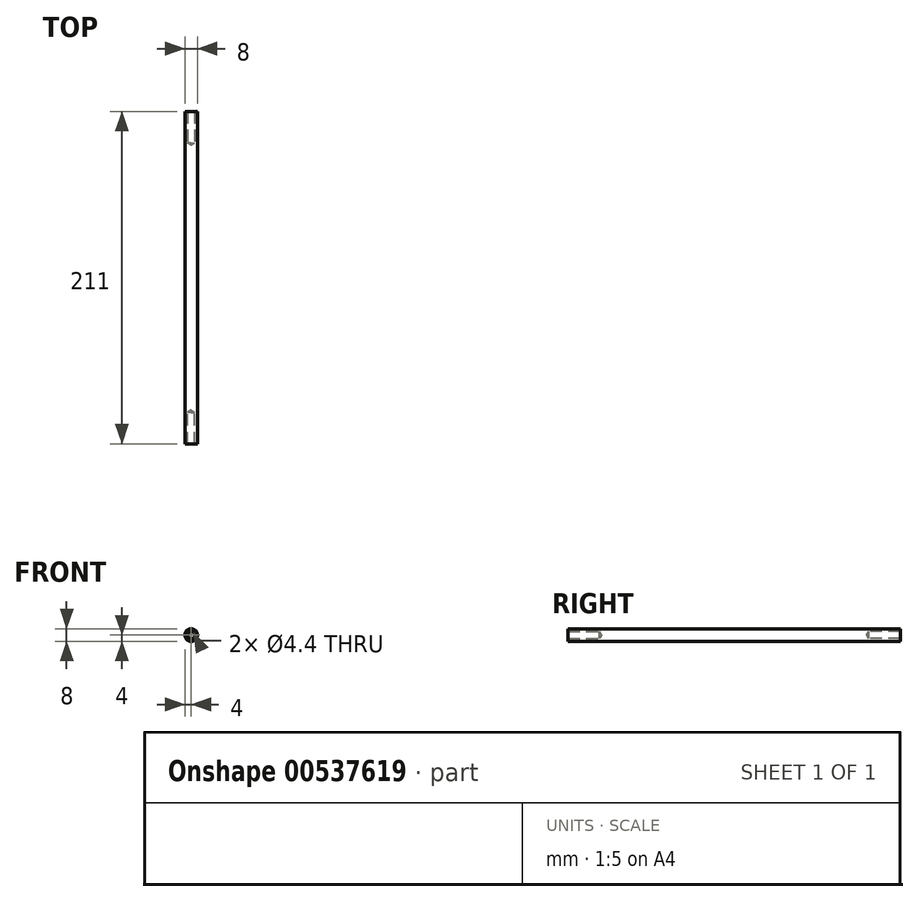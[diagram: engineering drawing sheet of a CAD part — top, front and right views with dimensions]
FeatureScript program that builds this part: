
annotation { "Feature Type Name" : "Feature", "Feature Type Description" : "" }
export const myFeature = defineFeature(function(context is Context, id is Id, definition is map)
    precondition{}
    {
        {
            var Q0;
            Q0=qCreatedBy(makeId("Front.planeOp"),FACE);
            var sketch = newSketch(context, id + "F0", { "sketchPlane" : qUnion([Q0])});
            skCircle(sketch, "E0", {"center": v(0, 0) * mm, "radius": 4 * mm});
            skSolve(sketch);
        }
        {
            var Q0;
            Q0=makeQuery(id+"F0.imprint","IMPRINT",FACE,{"disambiguationData":[TD([[makeQuery(id+"F0.imprint","IMPRINT",EDGE,{"derivedFrom":sQuery(id+"F0.wireOp",EDGE,"E0")}),1.0]])]});
            extrude(context, id + "F1", {"entities" : qUnion([Q0]), "flatOperationType" : FlatOperationType.REMOVE, "depth" : 211 * mm, "offsetDistance" : 25 * mm, "domain" : OperationDomain.MODEL});
        }
        {
            var Q0;
            Q0=makeQuery(id+"F1.opExtrude","CAP_FACE",FACE,{"disambiguationData":[OSD([sQuery(id+"F0.wireOp",EDGE,"E0")])],"isStart":false});
            var sketch = newSketch(context, id + "F2", { "sketchPlane" : qUnion([Q0])});
            skPoint(sketch, "E1", {"position": v(0, 0) * mm});
            skSolve(sketch);
        }
        {
            var Q0;
            Q0=makeQuery(id+"F1.opExtrude","CAP_FACE",FACE,{"disambiguationData":[OSD([sQuery(id+"F0.wireOp",EDGE,"E0")])],"isStart":true});
            var sketch = newSketch(context, id + "F3", { "sketchPlane" : qUnion([Q0])});
            skPoint(sketch, "E2", {"position": v(0, 0) * mm});
            skSolve(sketch);
        }
        {
            var Q0;
            Q0=sQuery(id+"F3.wireOp",VERTEX,"E2");
            var Q1;
            Q1=sQuery(id+"F2.wireOp",VERTEX,"E1");
            var Q2;
            Q2=makeQuery(id+"F1.opExtrude","SWEPT_BODY",BODY,{"disambiguationData":[OSD([sQuery(id+"F0.wireOp",EDGE,"E0")])]});
            hole(context, id + "F4", {"style" : HoleStyle.SIMPLE, "endStyle" : HoleEndStyle.BLIND, "standardTappedOrClearance" : lookupTablePath({ "standard" : "ISO", "fit" : "Normal", "size" : "M4", "type" : "Clearance" }), "standardBlindInLast" : lookupTablePath({ "fit" : "Standard", "standard" : "ISO", "size" : "M4", "type" : "Clearance" }), "holeDiameter" : 4.4 * mm, "holeDepth" : 20 * mm, "isTappedThrough" : true, "tappedDepth" : 12 * mm, "tapClearance" : 3, "locations" : qUnion([Q0, Q1]), "scope" : qUnion([Q2])});
        }
    });
